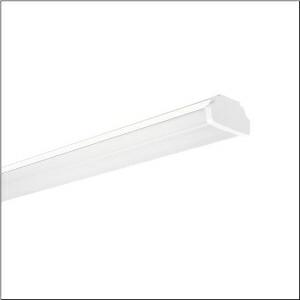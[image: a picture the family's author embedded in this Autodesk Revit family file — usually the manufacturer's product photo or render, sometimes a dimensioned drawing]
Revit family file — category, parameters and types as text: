
# Revit family: modario_31_gen_2_53bm812cv6c5d2_1f90
name_source: partatom
category: Lighting Fixtures
units: mm (PartAtom-declared; Revit-internal decimal feet)

## family parameters
Cut with Voids When Loaded = No
Host = Face
Light Source = No
Part Type = Normal
Room Calculation Point = No
Round Connector Dimension = Use Diameter
Shared = No

## types (1)
- --- (1 x LED, 12660 lm, 68.5 W, 6500K)
    Apparent Load = 69 VA
    CIE Flux Codes = 47 80 95 93 100
    Color Rendering = 80
    Color Temperature = 6500K
    Default Elevation = 1800 mm
    Description = Modario 31 Gen.2, luminaire insert, of sheet steel, coil coated, white, length: 1.495mm, width: 81mm, height: 82mm, 5x system unit, system units: 299mm, LED rated luminous flux: 12.660lm, light colour: 865, SDCM (Standard Deviation of Colour Matching)MacAdam ≤ 3 SDCM (initial), control gear: ON/OFF Multilumen, CLOi, with plug, 3-pole, with phase selection, mains connection: 220..240V, AC, 50/60Hz, start of lifetime: 69W, end of service life: 82W, through-wiring accessed according to module size, primary optical cover: cover, of PMMA, light emission: direct distribution, primary light characteristic: symmetric, protection rating (complete): IP20, protection rating (LED compartment): IP50, insulation class (complete): insulation class I (protective earthing), certification: CE, ENEC, VDE, UKCA, impact resistance: IK03, permissible ambient temperature for indoor applications: -35..+35°C, corresponds to IFS (International Featured Standards) requirements for safety and quality in the food industry, reducing of maximum allowable ambient temperature of 5°C with ceiling mounting, IP40 when using the optional accessory 5TP9018, packaging unit: 1 piece
    Height = 92 mm
    Lamp = 1 x LED
    Lamp Light Flux = 12660 lm
    Lamp Power = 68.5 W
    Lamp count = 1
    Length = 1495 mm
    Luminous efficacy = 185 lm/W
    Manufacturer = Siteco
    ModVariant = No
    Model = 53BM812CV6C5D2
    Mounting Place = Ceiling
    Mounting Type = Pendant
    Number of Poles = 1
    OnlyDefault = Yes
    Power Factor = 1
    Product Name = Modario 31 Gen.2
    Product group = luminaire insert | ceiling pendant
    ProductGroupID = 901
    Protection Class = Protection class I
    Protection Degree = IP 20
    RLX_Detail_Level = 1
    RLX_Emergency_Light_Flux = 0 lm
    RLX_Emergency_Type = 0
    RLX_Emergency_Type_DB = No
    RlxData = <blob elided: 40217 chars, md5=2557b8b6>
    Socket = socket
    Standby Power = 0 W
    System Light Flux = 12660 lm
    System Power = 69 W
    Type Comments = factory setting: luminous flux: 100 % | (A | C | E) | 161 mA
    Type Image = l_1341886.jpg
    URL = http://relux.com
    VarID = @adj_050737
    Voltage = 0 V
    Weight = 0.00 kg
    Width = 81 mm

## geometry (parser evidence)
native form markers: Blend x4, Sweep x12
no freeform markers — native parametric forms only
